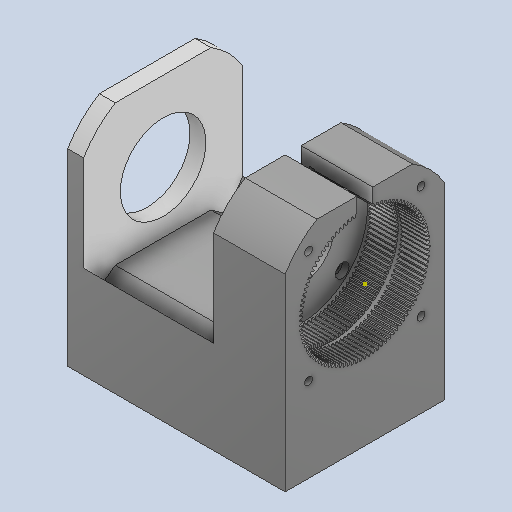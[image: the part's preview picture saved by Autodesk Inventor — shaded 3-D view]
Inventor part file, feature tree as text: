
AUTODESK INVENTOR PART (.ipt)
format: ipt  version: 2022 (Build 260153000, 153)  size: 1,497,600 bytes
history: mixed  units: mm
features: other x3, sketch x3, extrude x2, imported_body x1
ambient origin geometry x8: Origin, YZ Plane, XZ Plane, XY Plane, X Axis, Y Axis, Z Axis, Center Point
bodies: Solid1 (imported_parasolid)
feature tree (9):
  other  "Assembly2.iam"
  other  "96Gears_Stage_1_modified.ipt:1"
  other  "96Gears_Stage_2_modified.ipt:1"
  extrude  "Extrusion3"  Depth=3.0mm
  extrude  "Extrusion5"  Depth=6.0mm TaperAngle=0.0deg
  sketch  "Sketch5"  dims[d7=6.0mm d8=18.0mm d9=0.0mm]
  sketch  "Sketch4"  dims[d0=10.0mm d6=3.0mm]
  sketch  "Sketch7"  dims[d17=32.25mm d18=6.0mm d19=0.0mm]
  imported_body  NMx_Import_Brep_tag  [imported B-rep: ~787 faces, bbox_mm=[82.0, 83.027756, 60.0]]
